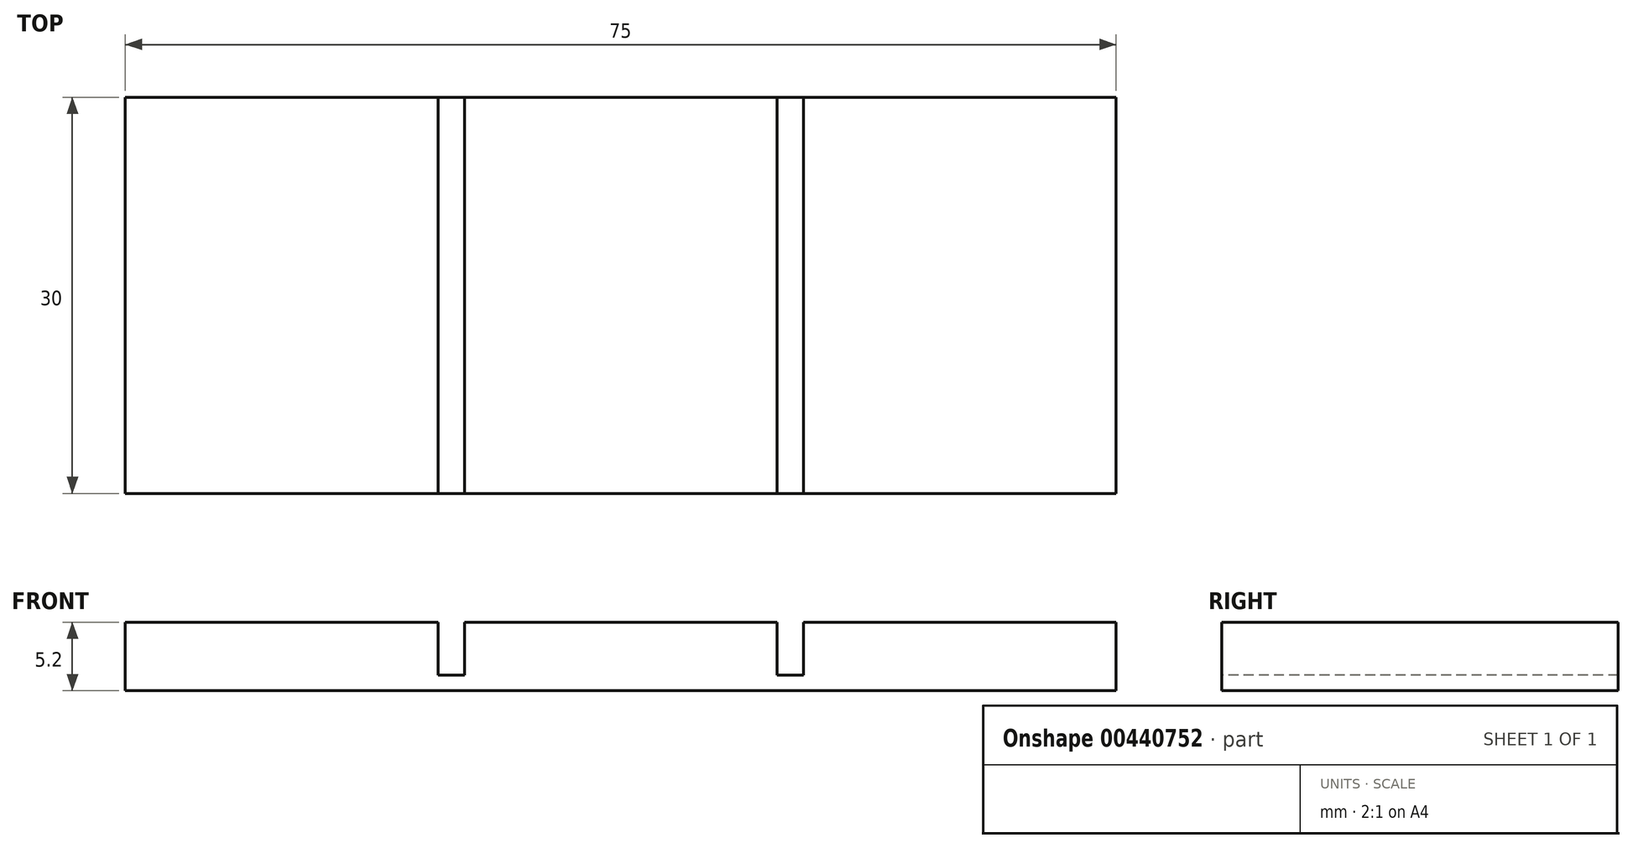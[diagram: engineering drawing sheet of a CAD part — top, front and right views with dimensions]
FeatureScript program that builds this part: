
annotation { "Feature Type Name" : "Feature", "Feature Type Description" : "" }
export const myFeature = defineFeature(function(context is Context, id is Id, definition is map)
    precondition{}
    {
        {
            var Q0;
            Q0=qCreatedBy(makeId("Top.planeOp"),FACE);
            var sketch = newSketch(context, id + "F0", { "sketchPlane" : qUnion([Q0])});
            skLineSegment(sketch, "E0.bottom", {"start": v(0, 0) * mm, "end": v(75, 0) * mm});
            skLineSegment(sketch, "E0.top", {"start": v(0, 30) * mm, "end": v(75, 30) * mm});
            skLineSegment(sketch, "E0.left", {"start": v(0, 0) * mm, "end": v(0, 30) * mm});
            skLineSegment(sketch, "E0.right", {"start": v(75, 0) * mm, "end": v(75, 30) * mm});
            skSolve(sketch);
        }
        {
            var Q0;
            Q0=makeQuery(id+"F0.imprint","IMPRINT",FACE,{"disambiguationData":[TD([[makeQuery(id+"F0.imprint","IMPRINT",EDGE,{"derivedFrom":sQuery(id+"F0.wireOp",EDGE,"E0.bottom")}),1.0]])]});
            extrude(context, id + "F1", {"entities" : qUnion([Q0]), "depth" : 1.2 * mm});
        }
        {
            var Q0;
            Q0=makeQuery(id+"F1.opExtrude","CAP_FACE",FACE,{"disambiguationData":[OSD([sQuery(id+"F0.wireOp",EDGE,"E0.bottom"),sQuery(id+"F0.wireOp",EDGE,"E0.top"),sQuery(id+"F0.wireOp",EDGE,"E0.left"),sQuery(id+"F0.wireOp",EDGE,"E0.right")])],"isStart":false});
            var sketch = newSketch(context, id + "F2", { "sketchPlane" : qUnion([Q0])});
            skLineSegment(sketch, "E1.bottom", {"start": v(0, 0) * mm, "end": v(23.67, 0) * mm});
            skLineSegment(sketch, "E1.top", {"start": v(0, 30) * mm, "end": v(23.67, 30) * mm});
            skLineSegment(sketch, "E1.left", {"start": v(0, 0) * mm, "end": v(0, 30) * mm});
            skLineSegment(sketch, "E1.right", {"start": v(23.67, 0) * mm, "end": v(23.67, 30) * mm});
            skLineSegment(sketch, "E2.bottom", {"start": v(25.67, 30) * mm, "end": v(49.33, 30) * mm});
            skLineSegment(sketch, "E2.top", {"start": v(25.67, 0) * mm, "end": v(49.33, 0) * mm});
            skLineSegment(sketch, "E2.left", {"start": v(25.67, 30) * mm, "end": v(25.67, 0) * mm});
            skLineSegment(sketch, "E2.right", {"start": v(49.33, 30) * mm, "end": v(49.33, 0) * mm});
            skLineSegment(sketch, "E3.bottom", {"start": v(75, 30) * mm, "end": v(51.33, 30) * mm});
            skLineSegment(sketch, "E3.top", {"start": v(75, 0) * mm, "end": v(51.33, 0) * mm});
            skLineSegment(sketch, "E3.left", {"start": v(75, 30) * mm, "end": v(75, 0) * mm});
            skLineSegment(sketch, "E3.right", {"start": v(51.33, 30) * mm, "end": v(51.33, 0) * mm});
            skSolve(sketch);
        }
        {
            var Q0;
            Q0=qSketchRegion(id+"F2",true);
            extrude(context, id + "F3", {"entities" : qUnion([Q0]), "operationType" : NewBodyOperationType.ADD, "depth" : 4 * mm});
        }
    });
